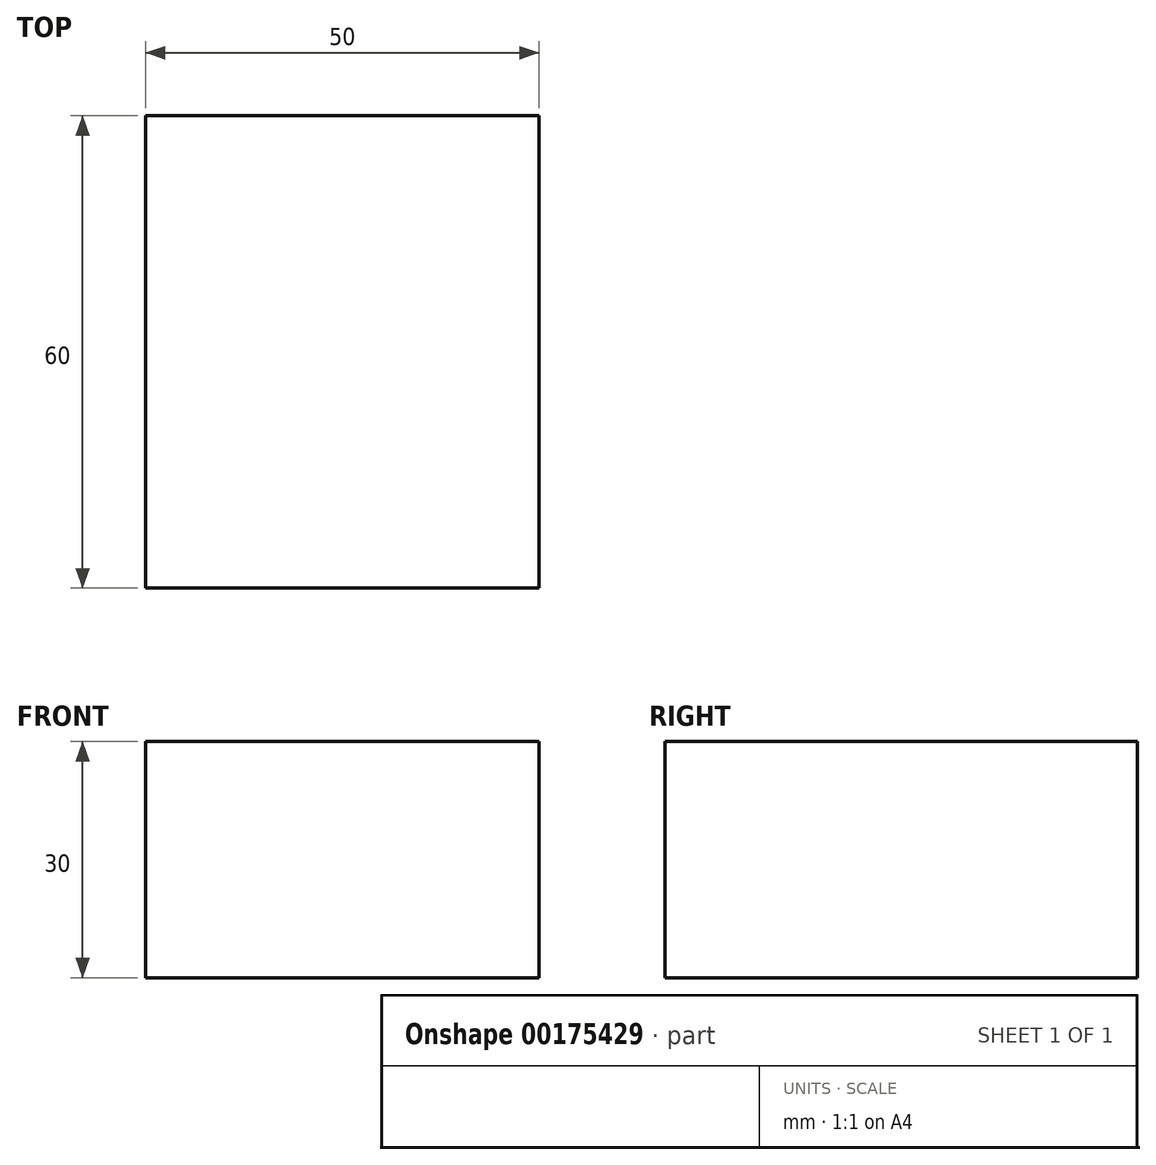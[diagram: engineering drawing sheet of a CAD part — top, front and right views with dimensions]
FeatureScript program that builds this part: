
annotation { "Feature Type Name" : "Feature", "Feature Type Description" : "" }
export const myFeature = defineFeature(function(context is Context, id is Id, definition is map)
    precondition{}
    {
        {
            var Q0;
            Q0=qCreatedBy(makeId("Top.planeOp"),FACE);
            var sketch = newSketch(context, id + "F0", { "sketchPlane" : qUnion([Q0])});
            skLineSegment(sketch, "E0.bottom", {"start": v(-26.9, 35) * mm, "end": v(23.1, 35) * mm});
            skLineSegment(sketch, "E0.top", {"start": v(-26.9, -25) * mm, "end": v(23.1, -25) * mm});
            skLineSegment(sketch, "E0.left", {"start": v(-26.9, 35) * mm, "end": v(-26.9, -25) * mm});
            skLineSegment(sketch, "E0.right", {"start": v(23.1, 35) * mm, "end": v(23.1, -25) * mm});
            skSolve(sketch);
        }
        {
            var Q0;
            Q0=makeQuery(id+"F0.imprint","IMPRINT",FACE,{"disambiguationData":[TD([[makeQuery(id+"F0.imprint","IMPRINT",EDGE,{"derivedFrom":sQuery(id+"F0.wireOp",EDGE,"E0.bottom")}),-1.0]])]});
            extrude(context, id + "F1", {"entities" : qUnion([Q0]), "depth" : 30 * mm});
        }
    });
